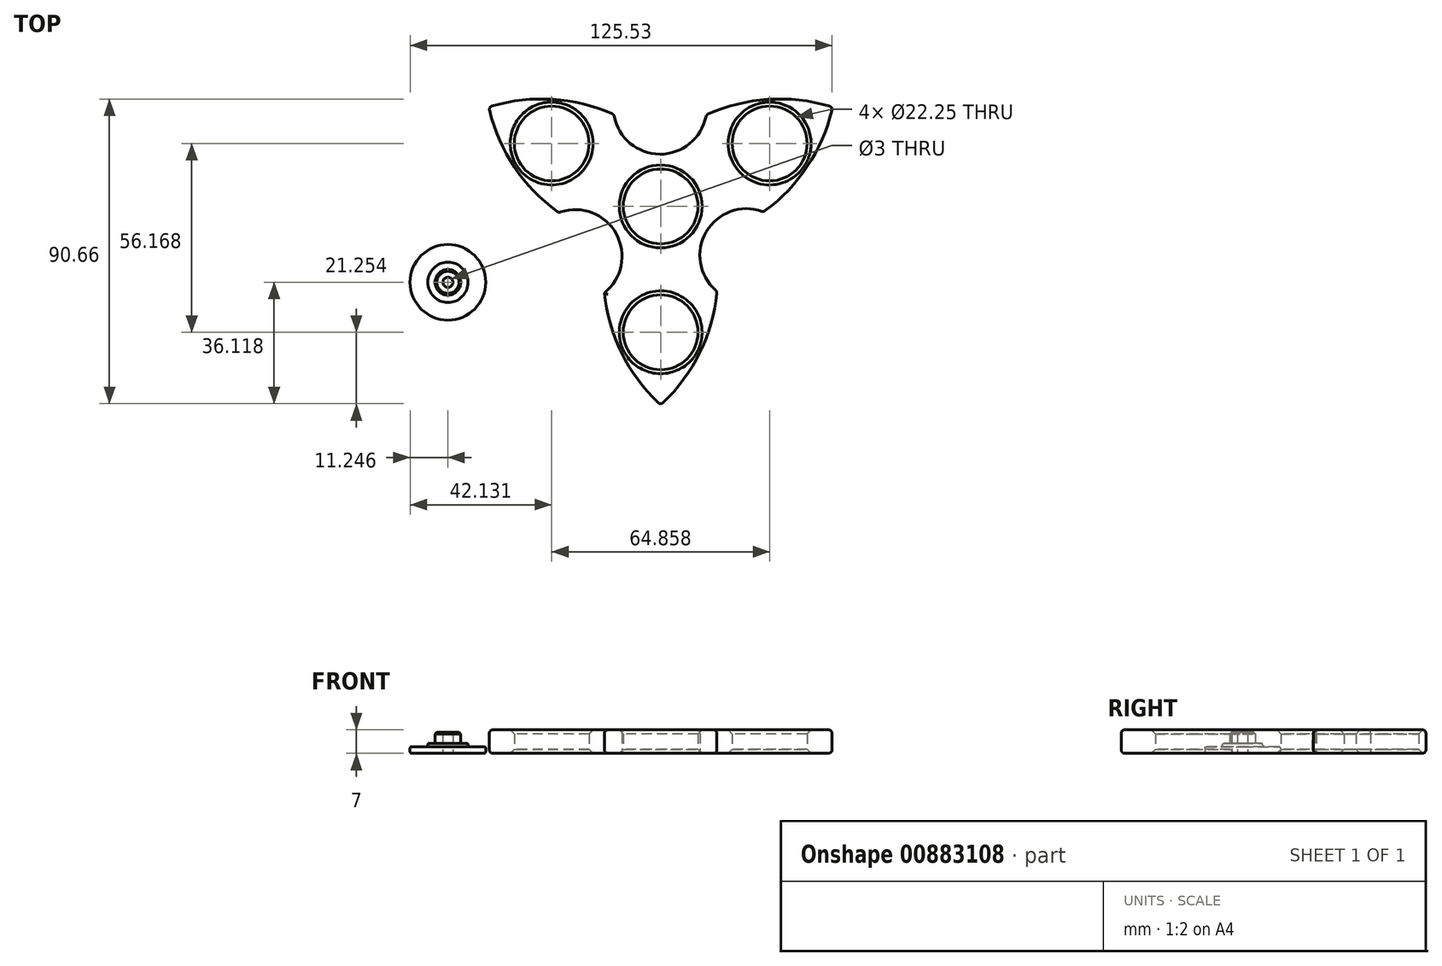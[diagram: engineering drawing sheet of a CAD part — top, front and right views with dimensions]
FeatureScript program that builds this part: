
annotation { "Feature Type Name" : "Feature", "Feature Type Description" : "" }
export const myFeature = defineFeature(function(context is Context, id is Id, definition is map)
    precondition{}
    {
        {
            var Q0;
            Q0=qCreatedBy(makeId("Top.planeOp"),FACE);
            var sketch = newSketch(context, id + "F0", { "sketchPlane" : qUnion([Q0])});
            skCircle(sketch, "E0", {"center": v(0, 0) * mm, "radius": 11.12 * mm});
            skArc(sketch, "E1", {"start": v(-51.15, 29.53) * mm, "mid": v(-43.66, 11.9) * mm, "end": v(-30.33, -1.85) * mm});
            skArc(sketch, "E2.1.1", {"start": v(0, -59.07) * mm, "mid": v(11.52, -43.77) * mm, "end": v(16.77, -25.35) * mm});
            skArc(sketch, "E2.2.1", {"start": v(-16.73, -25.74) * mm, "mid": v(-11.43, -43.94) * mm, "end": v(0, -59.07) * mm});
            skCircle(sketch, "E3", {"center": v(0, -37.45) * mm, "radius": 11.12 * mm});
            skArc(sketch, "E4.trimOffspring", {"start": v(30.65, -1.62) * mm, "mid": v(43.77, 12.07) * mm, "end": v(51.15, 29.53) * mm});
            skArc(sketch, "E5.trimOffspring", {"start": v(-13.93, 27.36) * mm, "mid": v(-32.34, 31.87) * mm, "end": v(-51.15, 29.53) * mm});
            skArc(sketch, "E6.trimOffspring", {"start": v(51.15, 29.53) * mm, "mid": v(32.14, 31.86) * mm, "end": v(13.57, 27.2) * mm});
            skCircle(sketch, "E7.1.0", {"center": v(32.43, 18.72) * mm, "radius": 11.12 * mm});
            skCircle(sketch, "E7.2.0", {"center": v(-32.43, 18.72) * mm, "radius": 11.12 * mm});
            skArc(sketch, "E8", {"start": v(30.65, -1.62) * mm, "mid": v(13.57, -7.55) * mm, "end": v(16.77, -25.35) * mm});
            skArc(sketch, "E9.1.0", {"start": v(-13.93, 27.36) * mm, "mid": v(-0.25, 15.53) * mm, "end": v(13.57, 27.2) * mm});
            skArc(sketch, "E9.2.0", {"start": v(-16.73, -25.74) * mm, "mid": v(-13.32, -7.98) * mm, "end": v(-30.33, -1.85) * mm});
            skSolve(sketch);
        }
        {
            var Q0;
            Q0=makeQuery(id+"F0.imprint","IMPRINT",FACE,{"disambiguationData":[TD([[makeQuery(id+"F0.imprint","IMPRINT",EDGE,{"derivedFrom":sQuery(id+"F0.wireOp",EDGE,"E0")}),-1.0]])]});
            extrude(context, id + "F1", {"entities" : qUnion([Q0]), "depth" : 7 * mm, "offsetDistance" : 25 * mm});
        }
        {
            var Q0;
            Q0=makeQuery(id+"F1.opExtrude","CAP_EDGE",EDGE,{"disambiguationData":[OSD([sQuery(id+"F0.wireOp",EDGE,"E1")])],"isStart":false});
            var Q1;
            Q1=makeQuery(id+"F1.opExtrude","CAP_EDGE",EDGE,{"disambiguationData":[OSD([sQuery(id+"F0.wireOp",EDGE,"E1")])],"isStart":true});
            var Q2;
            Q2=makeQuery(id+"F1.opExtrude","CAP_EDGE",EDGE,{"disambiguationData":[OSD([sQuery(id+"F0.wireOp",EDGE,"E2.2.1")])],"isStart":true});
            var Q3;
            Q3=makeQuery(id+"F1.opExtrude","CAP_EDGE",EDGE,{"disambiguationData":[OSD([sQuery(id+"F0.wireOp",EDGE,"E2.2.1")])],"isStart":false});
            var Q4;
            Q4=makeQuery(id+"F1.opExtrude","CAP_EDGE",EDGE,{"disambiguationData":[OSD([sQuery(id+"F0.wireOp",EDGE,"E9.2.0")])],"isStart":false});
            var Q5;
            Q5=makeQuery(id+"F1.opExtrude","CAP_EDGE",EDGE,{"disambiguationData":[OSD([sQuery(id+"F0.wireOp",EDGE,"E9.2.0")])],"isStart":true});
            var Q6;
            Q6=makeQuery(id+"F1.opExtrude","SWEPT_EDGE",EDGE,{"disambiguationData":[OSD([sQuery(id+"F0.wireOp",EDGE,"E1"),sQuery(id+"F0.wireOp",EDGE,"E9.2.0")])]});
            var Q7;
            Q7=makeQuery(id+"F1.opExtrude","CAP_EDGE",EDGE,{"disambiguationData":[OSD([sQuery(id+"F0.wireOp",EDGE,"E2.1.1")])],"isStart":true});
            var Q8;
            Q8=makeQuery(id+"F1.opExtrude","CAP_EDGE",EDGE,{"disambiguationData":[OSD([sQuery(id+"F0.wireOp",EDGE,"E2.1.1")])],"isStart":false});
            var Q9;
            Q9=makeQuery(id+"F1.opExtrude","SWEPT_EDGE",EDGE,{"disambiguationData":[OSD([sQuery(id+"F0.wireOp",EDGE,"E2.1.1"),sQuery(id+"F0.wireOp",EDGE,"E8")])]});
            var Q10;
            Q10=makeQuery(id+"F1.opExtrude","CAP_EDGE",EDGE,{"disambiguationData":[OSD([sQuery(id+"F0.wireOp",EDGE,"E8")])],"isStart":true});
            var Q11;
            Q11=makeQuery(id+"F1.opExtrude","CAP_EDGE",EDGE,{"disambiguationData":[OSD([sQuery(id+"F0.wireOp",EDGE,"E8")])],"isStart":false});
            var Q12;
            Q12=makeQuery(id+"F1.opExtrude","SWEPT_EDGE",EDGE,{"disambiguationData":[OSD([sQuery(id+"F0.wireOp",EDGE,"E4.trimOffspring"),sQuery(id+"F0.wireOp",EDGE,"E8")])]});
            var Q13;
            Q13=makeQuery(id+"F1.opExtrude","CAP_EDGE",EDGE,{"disambiguationData":[OSD([sQuery(id+"F0.wireOp",EDGE,"E4.trimOffspring")])],"isStart":false});
            var Q14;
            Q14=makeQuery(id+"F1.opExtrude","CAP_EDGE",EDGE,{"disambiguationData":[OSD([sQuery(id+"F0.wireOp",EDGE,"E4.trimOffspring")])],"isStart":true});
            var Q15;
            Q15=makeQuery(id+"F1.opExtrude","CAP_EDGE",EDGE,{"disambiguationData":[OSD([sQuery(id+"F0.wireOp",EDGE,"E5.trimOffspring")])],"isStart":false});
            var Q16;
            Q16=makeQuery(id+"F1.opExtrude","CAP_EDGE",EDGE,{"disambiguationData":[OSD([sQuery(id+"F0.wireOp",EDGE,"E9.1.0")])],"isStart":false});
            var Q17;
            Q17=makeQuery(id+"F1.opExtrude","SWEPT_EDGE",EDGE,{"disambiguationData":[OSD([sQuery(id+"F0.wireOp",EDGE,"E5.trimOffspring"),sQuery(id+"F0.wireOp",EDGE,"E9.1.0")])]});
            var Q18;
            Q18=makeQuery(id+"F1.opExtrude","CAP_EDGE",EDGE,{"disambiguationData":[OSD([sQuery(id+"F0.wireOp",EDGE,"E6.trimOffspring")])],"isStart":false});
            var Q19;
            Q19=makeQuery(id+"F1.opExtrude","SWEPT_EDGE",EDGE,{"disambiguationData":[OSD([sQuery(id+"F0.wireOp",EDGE,"E2.1.1"),sQuery(id+"F0.wireOp",EDGE,"E2.2.1")])]});
            var Q20;
            Q20=makeQuery(id+"F1.opExtrude","SWEPT_EDGE",EDGE,{"disambiguationData":[OSD([sQuery(id+"F0.wireOp",EDGE,"E4.trimOffspring"),sQuery(id+"F0.wireOp",EDGE,"E6.trimOffspring")])]});
            var Q21;
            Q21=makeQuery(id+"F1.opExtrude","CAP_EDGE",EDGE,{"disambiguationData":[OSD([sQuery(id+"F0.wireOp",EDGE,"E6.trimOffspring")])],"isStart":true});
            var Q22;
            Q22=makeQuery(id+"F1.opExtrude","SWEPT_EDGE",EDGE,{"disambiguationData":[OSD([sQuery(id+"F0.wireOp",EDGE,"E6.trimOffspring"),sQuery(id+"F0.wireOp",EDGE,"E9.1.0")])]});
            var Q23;
            Q23=makeQuery(id+"F1.opExtrude","CAP_EDGE",EDGE,{"disambiguationData":[OSD([sQuery(id+"F0.wireOp",EDGE,"E5.trimOffspring")])],"isStart":true});
            var Q24;
            Q24=makeQuery(id+"F1.opExtrude","CAP_EDGE",EDGE,{"disambiguationData":[OSD([sQuery(id+"F0.wireOp",EDGE,"E9.1.0")])],"isStart":true});
            var Q25;
            Q25=makeQuery(id+"F1.opExtrude","SWEPT_EDGE",EDGE,{"disambiguationData":[OSD([sQuery(id+"F0.wireOp",EDGE,"E1"),sQuery(id+"F0.wireOp",EDGE,"E5.trimOffspring")])]});
            fillet(context, id + "F2", {"entities" : qUnion([Q0, Q1, Q2, Q3, Q4, Q5, Q6, Q7, Q8, Q9, Q10, Q11, Q12, Q13, Q14, Q15, Q16, Q17, Q18, Q19, Q20, Q21, Q22, Q23, Q24, Q25]), "radius" : 1 * mm, "tangentPropagation" : true, "allowEdgeOverflow" : false});
        }
        {
            var Q0;
            Q0=makeQuery(id+"F1.opExtrude","CAP_EDGE",EDGE,{"disambiguationData":[OSD([sQuery(id+"F0.wireOp",EDGE,"E7.2.0")])],"isStart":false});
            var Q1;
            Q1=makeQuery(id+"F1.opExtrude","CAP_EDGE",EDGE,{"disambiguationData":[OSD([sQuery(id+"F0.wireOp",EDGE,"E7.2.0")])],"isStart":true});
            var Q2;
            Q2=makeQuery(id+"F1.opExtrude","CAP_EDGE",EDGE,{"disambiguationData":[OSD([sQuery(id+"F0.wireOp",EDGE,"E7.1.0")])],"isStart":false});
            var Q3;
            Q3=makeQuery(id+"F1.opExtrude","CAP_EDGE",EDGE,{"disambiguationData":[OSD([sQuery(id+"F0.wireOp",EDGE,"E7.1.0")])],"isStart":true});
            var Q4;
            Q4=makeQuery(id+"F1.opExtrude","CAP_EDGE",EDGE,{"disambiguationData":[OSD([sQuery(id+"F0.wireOp",EDGE,"E3")])],"isStart":false});
            var Q5;
            Q5=makeQuery(id+"F1.opExtrude","CAP_EDGE",EDGE,{"disambiguationData":[OSD([sQuery(id+"F0.wireOp",EDGE,"E3")])],"isStart":true});
            var Q6;
            Q6=makeQuery(id+"F1.opExtrude","CAP_EDGE",EDGE,{"disambiguationData":[OSD([sQuery(id+"F0.wireOp",EDGE,"E0")])],"isStart":false});
            var Q7;
            Q7=makeQuery(id+"F1.opExtrude","CAP_EDGE",EDGE,{"disambiguationData":[OSD([sQuery(id+"F0.wireOp",EDGE,"E0")])],"isStart":true});
            chamfer(context, id + "F3", {"entities" : qUnion([Q0, Q1, Q2, Q3, Q4, Q5, Q6, Q7]), "width" : 1.2 * mm, "tangentPropagation" : true});
        }
        {
            var Q0;
            Q0=qCreatedBy(makeId("Top.planeOp"),FACE);
            var sketch = newSketch(context, id + "F4", { "sketchPlane" : qUnion([Q0])});
            skCircle(sketch, "E10", {"center": v(-63.31, -22.58) * mm, "radius": 11.25 * mm});
            skCircle(sketch, "E11", {"center": v(-63.31, -22.58) * mm, "radius": 3.8 * mm});
            skCircle(sketch, "E12", {"center": v(-63.31, -22.58) * mm, "radius": 6 * mm});
            skCircle(sketch, "E13", {"center": v(-63.31, -22.58) * mm, "radius": 1.5 * mm});
            skSolve(sketch);
        }
        {
            var Q0;
            Q0=makeQuery(id+"F4.imprint","IMPRINT",FACE,{"disambiguationData":[TD([[makeQuery(id+"F4.imprint","IMPRINT",EDGE,{"derivedFrom":sQuery(id+"F4.wireOp",EDGE,"E11")}),1.0]])]});
            extrude(context, id + "F5", {"entities" : qUnion([Q0]), "depth" : 6.25 * mm, "offsetDistance" : 25 * mm});
        }
        {
            var Q0;
            Q0=makeQuery(id+"F4.imprint","IMPRINT",FACE,{"disambiguationData":[TD([[makeQuery(id+"F4.imprint","IMPRINT",EDGE,{"derivedFrom":sQuery(id+"F4.wireOp",EDGE,"E11")}),-1.0]])]});
            extrude(context, id + "F6", {"entities" : qUnion([Q0]), "operationType" : NewBodyOperationType.ADD, "depth" : 3 * mm, "offsetDistance" : 25 * mm});
        }
        {
            var Q0;
            Q0=makeQuery(id+"F4.imprint","IMPRINT",FACE,{"disambiguationData":[TD([[makeQuery(id+"F4.imprint","IMPRINT",EDGE,{"derivedFrom":sQuery(id+"F4.wireOp",EDGE,"E10")}),1.0]])]});
            extrude(context, id + "F7", {"entities" : qUnion([Q0]), "operationType" : NewBodyOperationType.ADD, "depth" : 2 * mm, "offsetDistance" : 25 * mm});
        }
        {
            var Q0;
            Q0=makeQuery(id+"F5.opExtrude","CAP_EDGE",EDGE,{"disambiguationData":[OSD([sQuery(id+"F4.wireOp",EDGE,"E11")])],"isStart":false});
            chamfer(context, id + "F8", {"entities" : qUnion([Q0]), "width" : 0.5 * mm, "tangentPropagation" : true});
        }
        {
            var Q0;
            Q0=makeQuery(id+"F6.opExtrude","CAP_EDGE",EDGE,{"disambiguationData":[OSD([sQuery(id+"F4.wireOp",EDGE,"E12")])],"isStart":false});
            var Q1;
            Q1=makeQuery(id+"F7.opExtrude","CAP_EDGE",EDGE,{"disambiguationData":[OSD([sQuery(id+"F4.wireOp",EDGE,"E10")])],"isStart":false});
            var Q2;
            Q2=makeQuery(id+"F7.opExtrude","CAP_EDGE",EDGE,{"disambiguationData":[OSD([sQuery(id+"F4.wireOp",EDGE,"E10")])],"isStart":true});
            var Q3;
            Q3=makeQuery(id+"F6.opExtrude","SWEPT_FACE",FACE,{"disambiguationData":[OSD([sQuery(id+"F4.wireOp",EDGE,"E12")])]});
            fillet(context, id + "F9", {"entities" : qUnion([Q0, Q1, Q2, Q3]), "radius" : 0.5 * mm, "tangentPropagation" : true, "allowEdgeOverflow" : false});
        }
        {
            var Q0;
            Q0=makeQuery(id+"F5.opExtrude","CAP_EDGE",EDGE,{"disambiguationData":[OSD([sQuery(id+"F4.wireOp",EDGE,"E13")])],"isStart":true});
            var Q1;
            Q1=makeQuery(id+"F5.opExtrude","SWEPT_FACE",FACE,{"disambiguationData":[OSD([sQuery(id+"F4.wireOp",EDGE,"E13")])]});
            fillet(context, id + "F10", {"entities" : qUnion([Q0, Q1]), "radius" : 0.5 * mm, "tangentPropagation" : true, "allowEdgeOverflow" : false});
        }
    });
